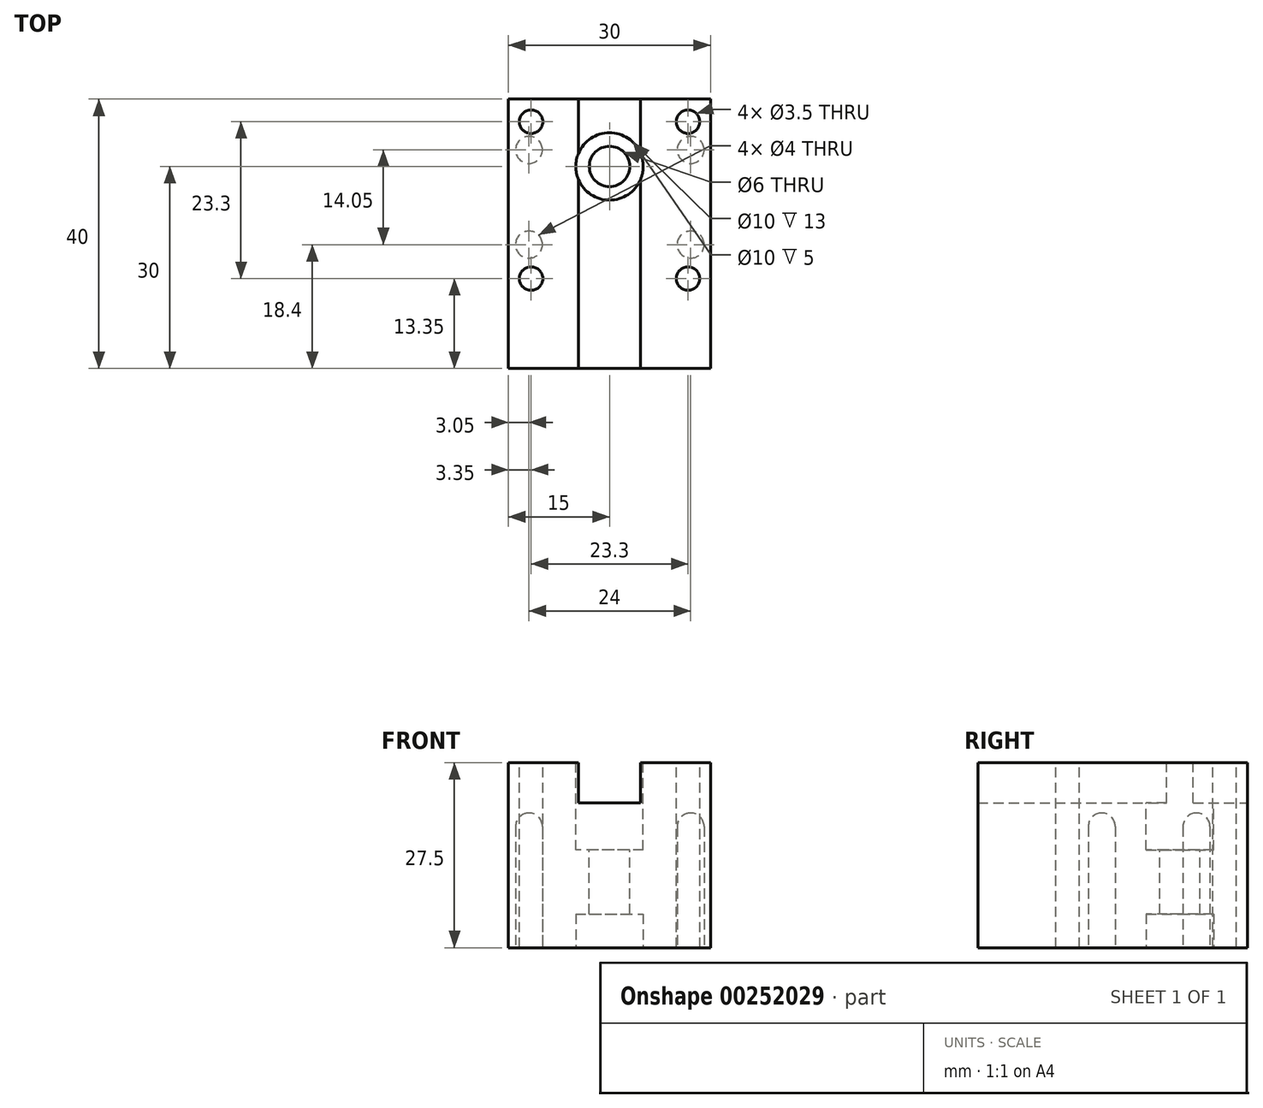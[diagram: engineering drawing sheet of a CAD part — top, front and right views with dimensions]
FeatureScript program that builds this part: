
annotation { "Feature Type Name" : "Feature", "Feature Type Description" : "" }
export const myFeature = defineFeature(function(context is Context, id is Id, definition is map)
    precondition{}
    {
        {
            var Q0;
            Q0=qCreatedBy(makeId("Top.planeOp"),FACE);
            var sketch = newSketch(context, id + "F0", { "sketchPlane" : qUnion([Q0])});
            skLineSegment(sketch, "E0.bottom", {"start": v(15, -20) * mm, "end": v(-15, -20) * mm});
            skLineSegment(sketch, "E0.top", {"start": v(15, 20) * mm, "end": v(-15, 20) * mm});
            skLineSegment(sketch, "E0.left", {"start": v(15, -20) * mm, "end": v(15, 20) * mm});
            skLineSegment(sketch, "E0.right", {"start": v(-15, -20) * mm, "end": v(-15, 20) * mm});
            skPoint(sketch, "E0.middle", {"position": v(0, 0) * mm});
            skSolve(sketch);
        }
        {
            var Q0;
            Q0 = qSketchRegion(id + "F0", true);
            extrude(context, id + "F1", {"entities" : qUnion([Q0]), "depth" : 27.5 * mm});
        }
        {
            var Q0;
            Q0=makeQuery(id+"F1.opExtrude","CAP_FACE",FACE,{"disambiguationData":[OSD([sQuery(id+"F0.wireOp",EDGE,"E0.bottom"),sQuery(id+"F0.wireOp",EDGE,"E0.top"),sQuery(id+"F0.wireOp",EDGE,"E0.left"),sQuery(id+"F0.wireOp",EDGE,"E0.right")])],"isStart":false});
            var sketch = newSketch(context, id + "F2", { "sketchPlane" : qUnion([Q0])});
            skLineSegment(sketch, "E1.bottom", {"start": v(4.6, -20) * mm, "end": v(-4.6, -20) * mm});
            skLineSegment(sketch, "E1.top", {"start": v(4.6, 20) * mm, "end": v(-4.6, 20) * mm});
            skLineSegment(sketch, "E1.left", {"start": v(4.6, -20) * mm, "end": v(4.6, 20) * mm});
            skLineSegment(sketch, "E1.right", {"start": v(-4.6, -20) * mm, "end": v(-4.6, 20) * mm});
            skPoint(sketch, "E1.middle", {"position": v(0, 0) * mm});
            skSolve(sketch);
        }
        {
            var Q0;
            Q0 = qSketchRegion(id + "F2", true);
            extrude(context, id + "F3", {"entities" : qUnion([Q0]), "operationType" : NewBodyOperationType.REMOVE, "oppositeDirection" : true, "depth" : 6 * mm});
        }
        {
            var Q0;
            {var subQ0=sQuery(id+"F0.wireOp",EDGE,"E0.bottom");var subQ1=sQuery(id+"F0.wireOp",EDGE,"E0.right");var subQ2=sQuery(id+"F0.wireOp",EDGE,"E0.top");Q0=makeQuery(id+"F3.boolean.opBoolean","SPLIT",FACE,{"disambiguationData":[TD([makeQuery(id+"F1.opExtrude","SWEPT_FACE",FACE,{"disambiguationData":[OSD([subQ1])]})])],"derivedFrom":makeQuery(id+"F1.opExtrude","CAP_FACE",FACE,{"disambiguationData":[OSD([subQ0,subQ2,sQuery(id+"F0.wireOp",EDGE,"E0.left"),subQ1])],"isStart":false})});}
            var sketch = newSketch(context, id + "F4", { "sketchPlane" : qUnion([Q0])});
            skCircle(sketch, "E2", {"center": v(-11.65, 16.65) * mm, "radius": 1.75 * mm});
            skCircle(sketch, "E3", {"center": v(-11.65, -6.65) * mm, "radius": 1.75 * mm});
            skCircle(sketch, "E4", {"center": v(11.65, 16.65) * mm, "radius": 1.75 * mm});
            skCircle(sketch, "E5", {"center": v(11.65, -6.65) * mm, "radius": 1.75 * mm});
            skSolve(sketch);
        }
        {
            var Q0;
            Q0 = qSketchRegion(id + "F4", true);
            extrude(context, id + "F5", {"entities" : qUnion([Q0]), "operationType" : NewBodyOperationType.REMOVE, "endBound" : BoundingType.THROUGH_ALL, "oppositeDirection" : true, "depth" : 25 * mm});
        }
        {
            var Q0;
            Q0=makeQuery(id+"F3.boolean.opBoolean","COPY",FACE,{"derivedFrom":makeQuery(id+"F3.opExtrude","CAP_FACE",FACE,{"disambiguationData":[OSD([sQuery(id+"F2.wireOp",EDGE,"E1.bottom"),sQuery(id+"F2.wireOp",EDGE,"E1.top"),sQuery(id+"F2.wireOp",EDGE,"E1.left"),sQuery(id+"F2.wireOp",EDGE,"E1.right")])],"isStart":false})});
            var sketch = newSketch(context, id + "F6", { "sketchPlane" : qUnion([Q0])});
            skCircle(sketch, "E6", {"center": v(0, 10) * mm, "radius": 3 * mm});
            skSolve(sketch);
        }
        {
            var Q0;
            Q0 = qSketchRegion(id + "F6", true);
            extrude(context, id + "F7", {"entities" : qUnion([Q0]), "operationType" : NewBodyOperationType.REMOVE, "endBound" : BoundingType.THROUGH_ALL, "oppositeDirection" : true, "depth" : 25 * mm});
        }
        {
            var Q0;
            {var subQ0=sQuery(id+"F0.wireOp",EDGE,"E0.bottom");var subQ1=sQuery(id+"F0.wireOp",EDGE,"E0.right");var subQ2=sQuery(id+"F0.wireOp",EDGE,"E0.top");Q0=makeQuery(id+"F3.boolean.opBoolean","SPLIT",FACE,{"disambiguationData":[TD([makeQuery(id+"F1.opExtrude","SWEPT_FACE",FACE,{"disambiguationData":[OSD([subQ1])]})])],"derivedFrom":makeQuery(id+"F1.opExtrude","CAP_FACE",FACE,{"disambiguationData":[OSD([subQ0,subQ2,sQuery(id+"F0.wireOp",EDGE,"E0.left"),subQ1])],"isStart":false})});}
            var sketch = newSketch(context, id + "F8", { "sketchPlane" : qUnion([Q0])});
            skCircle(sketch, "E7", {"center": v(0, 10) * mm, "radius": 5 * mm});
            skSolve(sketch);
        }
        {
            var Q0;
            Q0 = qSketchRegion(id + "F8", true);
            extrude(context, id + "F9", {"entities" : qUnion([Q0]), "operationType" : NewBodyOperationType.REMOVE, "oppositeDirection" : true, "depth" : 13 * mm});
        }
        {
            var Q0;
            Q0=makeQuery(id+"F1.opExtrude","CAP_FACE",FACE,{"disambiguationData":[OSD([sQuery(id+"F0.wireOp",EDGE,"E0.bottom"),sQuery(id+"F0.wireOp",EDGE,"E0.top"),sQuery(id+"F0.wireOp",EDGE,"E0.left"),sQuery(id+"F0.wireOp",EDGE,"E0.right")])],"isStart":true});
            var sketch = newSketch(context, id + "F10", { "sketchPlane" : qUnion([Q0])});
            skCircle(sketch, "E8", {"center": v(0, -10) * mm, "radius": 5 * mm});
            skSolve(sketch);
        }
        {
            var Q0;
            Q0 = qSketchRegion(id + "F10", true);
            extrude(context, id + "F11", {"entities" : qUnion([Q0]), "operationType" : NewBodyOperationType.REMOVE, "oppositeDirection" : true, "depth" : 5 * mm});
        }
        {
            var Q0;
            Q0=makeQuery(id+"F1.opExtrude","CAP_FACE",FACE,{"disambiguationData":[OSD([sQuery(id+"F0.wireOp",EDGE,"E0.bottom"),sQuery(id+"F0.wireOp",EDGE,"E0.top"),sQuery(id+"F0.wireOp",EDGE,"E0.left"),sQuery(id+"F0.wireOp",EDGE,"E0.right")])],"isStart":true});
            var sketch = newSketch(context, id + "F12", { "sketchPlane" : qUnion([Q0])});
            skCircle(sketch, "E9", {"center": v(-11.95, 1.6) * mm, "radius": 2 * mm});
            skCircle(sketch, "E10", {"center": v(-11.95, -12.45) * mm, "radius": 2 * mm});
            skCircle(sketch, "E11", {"center": v(12.05, 1.6) * mm, "radius": 2 * mm});
            skCircle(sketch, "E12", {"center": v(12.05, -12.45) * mm, "radius": 2 * mm});
            skSolve(sketch);
        }
        {
            var Q0;
            Q0 = qSketchRegion(id + "F12", true);
            extrude(context, id + "F13", {"entities" : qUnion([Q0]), "operationType" : NewBodyOperationType.REMOVE, "oppositeDirection" : true, "depth" : 20 * mm});
        }
        {
            var Q0;
            Q0=makeQuery(id+"F13.boolean.opBoolean","COPY",FACE,{"derivedFrom":makeQuery(id+"F13.opExtrude","CAP_FACE",FACE,{"disambiguationData":[OSD([sQuery(id+"F12.wireOp",EDGE,"E9")])],"isStart":false})});
            var Q1;
            Q1=makeQuery(id+"F13.boolean.opBoolean","COPY",FACE,{"derivedFrom":makeQuery(id+"F13.opExtrude","CAP_FACE",FACE,{"disambiguationData":[OSD([sQuery(id+"F12.wireOp",EDGE,"E10")])],"isStart":false})});
            var Q2;
            Q2=makeQuery(id+"F13.boolean.opBoolean","COPY",FACE,{"derivedFrom":makeQuery(id+"F13.opExtrude","CAP_FACE",FACE,{"disambiguationData":[OSD([sQuery(id+"F12.wireOp",EDGE,"E11")])],"isStart":false})});
            var Q3;
            Q3=makeQuery(id+"F13.boolean.opBoolean","COPY",FACE,{"derivedFrom":makeQuery(id+"F13.opExtrude","CAP_FACE",FACE,{"disambiguationData":[OSD([sQuery(id+"F12.wireOp",EDGE,"E12")])],"isStart":false})});
            fillet(context, id + "F14", {"entities" : qUnion([Q0, Q1, Q2, Q3]), "radius" : 2 * mm, "tangentPropagation" : true, "allowEdgeOverflow" : false});
        }
    });
